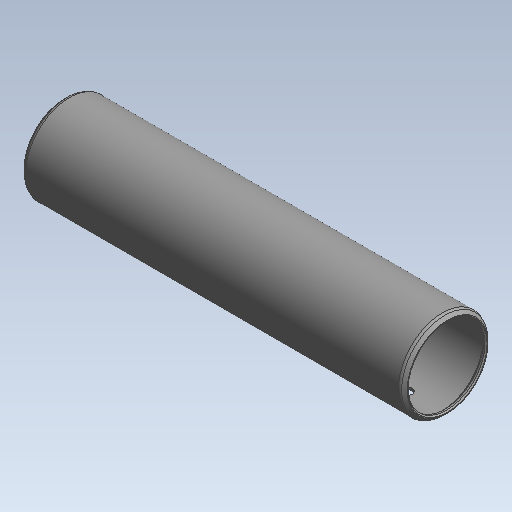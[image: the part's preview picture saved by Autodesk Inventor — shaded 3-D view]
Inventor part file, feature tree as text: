
AUTODESK INVENTOR PART (.ipt)
format: ipt  version: 2020 (Build 240168000, 168)  size: 146,432 bytes
history: native  units: mm (DEFAULTED — no unit token found)
features: other x42, sketch x2, revolve x1, extrude x1
ambient origin geometry x8: Origin, YZ Plane, XZ Plane, XY Plane, X Axis, Y Axis, Z Axis, Center Point
bodies: Solid1 (feature_tree)
feature tree (46):
  revolve  "Revolution1"  [1 undecoded]
  extrude  "Extrusion1"  [1 undecoded]
  other  "cp1_XY"
  other  "cp1_YZ"
  other  "cp1_ZX"
  other  "cp1_X"
  other  "cp1_Y"
  other  "cp1_Z"
  other  "cp1_Center"
  other  "cp2_XY"
  other  "cp2_YZ"
  other  "cp2_ZX"
  other  "cp2_X"
  other  "cp2_Y"
  other  "cp2_Z"
  other  "cp2_Center"
  other  "cp3_XY"
  other  "cp3_YZ"
  other  "cp3_ZX"
  other  "cp3_X"
  other  "cp3_Y"
  other  "cp3_Z"
  other  "cp3_Center"
  other  "cp4_XY"
  other  "cp4_YZ"
  other  "cp4_ZX"
  other  "cp4_X"
  other  "cp4_Y"
  other  "cp4_Z"
  other  "cp4_Center"
  other  "tube_front_XY"
  other  "tube_front_YZ"
  other  "tube_front_ZX"
  other  "tube_front_X"
  other  "tube_front_Y"
  other  "tube_front_Z"
  other  "tube_front_Center"
  other  "tube_rear_XY"
  other  "tube_rear_YZ"
  other  "tube_rear_ZX"
  other  "tube_rear_X"
  other  "tube_rear_Y"
  other  "tube_rear_Z"
  other  "tube_rear_Center"
  sketch  "Sketch_1"  dims[d0=360.0deg d1=10.2235mm d2=0.0mm]
  sketch  "Sketch_4"
note: 2 required parameter values undecoded (feature->parameter linkage not recoverable at this tier; creation-order binding heuristic only, values carry confidence <= 0.55)